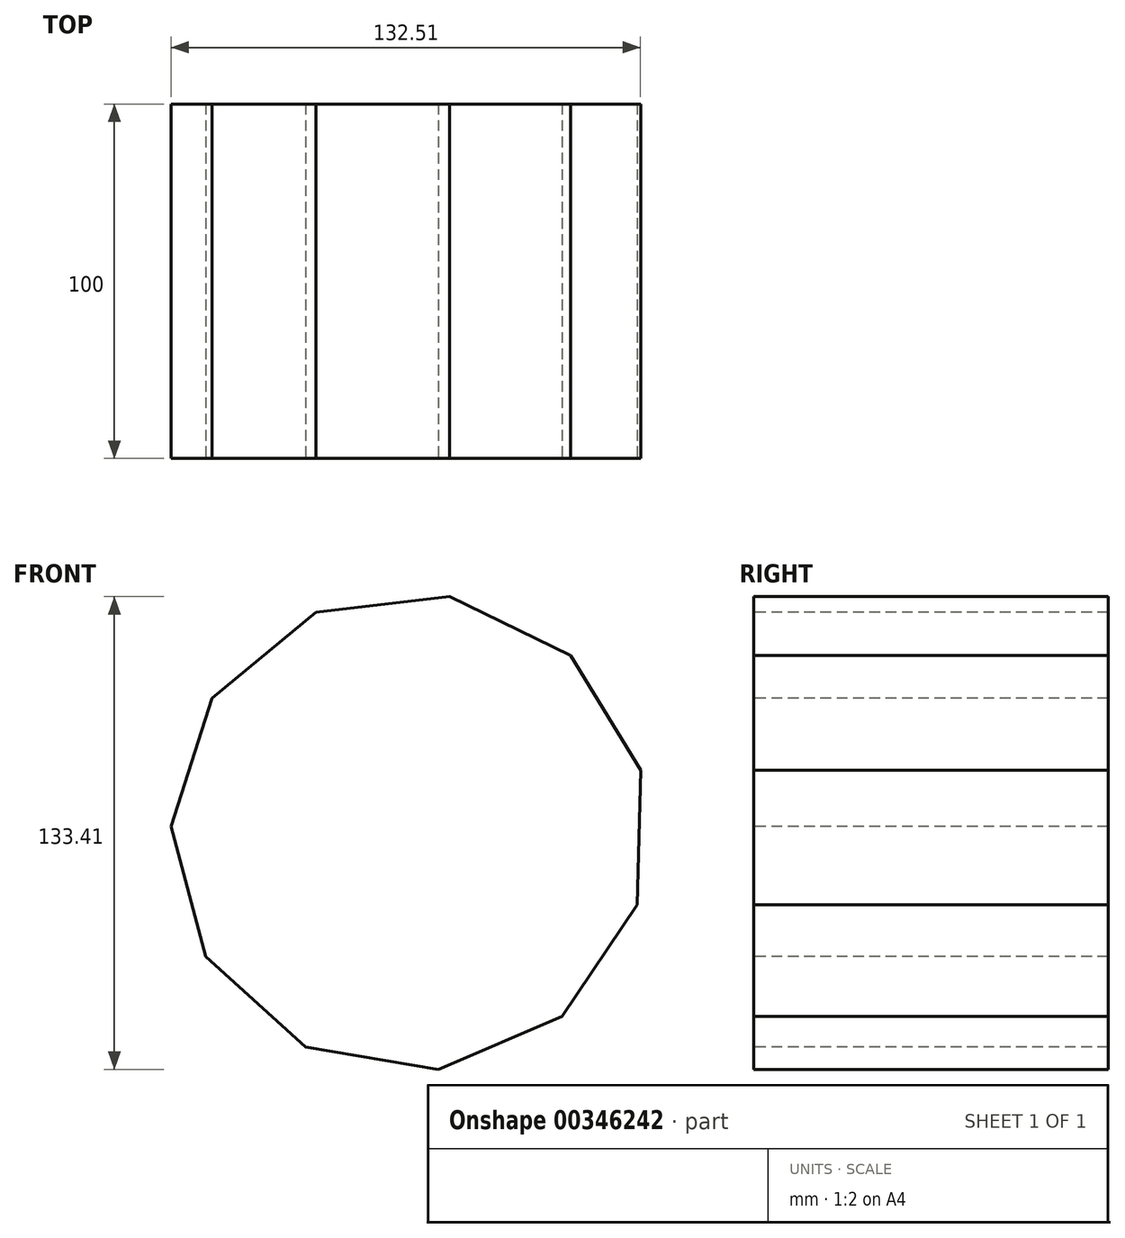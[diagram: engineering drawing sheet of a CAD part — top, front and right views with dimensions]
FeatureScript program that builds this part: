
annotation { "Feature Type Name" : "Feature", "Feature Type Description" : "" }
export const myFeature = defineFeature(function(context is Context, id is Id, definition is map)
    precondition{}
    {
        {
            var Q0;
            Q0=qCreatedBy(makeId("Front.planeOp"),FACE);
            var sketch = newSketch(context, id + "F0", { "sketchPlane" : qUnion([Q0])});
            skCircle(sketch, "E0.cCircle", {"center": v(0, 0) * mm, "radius": 67.41 * mm, "construction": true});
            skLineSegment(sketch, "E0.0", {"start": v(45.37, 49.86) * mm, "end": v(65.12, 17.42) * mm});
            skLineSegment(sketch, "E0.1", {"start": v(65.12, 17.42) * mm, "end": v(64.2, -20.55) * mm});
            skLineSegment(sketch, "E0.2", {"start": v(64.2, -20.55) * mm, "end": v(42.9, -52) * mm});
            skLineSegment(sketch, "E0.3", {"start": v(42.9, -52) * mm, "end": v(7.97, -66.94) * mm});
            skLineSegment(sketch, "E0.4", {"start": v(7.97, -66.94) * mm, "end": v(-29.48, -60.62) * mm});
            skLineSegment(sketch, "E0.5", {"start": v(-29.48, -60.62) * mm, "end": v(-57.58, -35.06) * mm});
            skLineSegment(sketch, "E0.6", {"start": v(-57.58, -35.06) * mm, "end": v(-67.4, 1.63) * mm});
            skLineSegment(sketch, "E0.7", {"start": v(-67.4, 1.63) * mm, "end": v(-55.8, 37.8) * mm});
            skLineSegment(sketch, "E0.8", {"start": v(-55.8, 37.8) * mm, "end": v(-26.5, 61.98) * mm});
            skLineSegment(sketch, "E0.9", {"start": v(-26.5, 61.98) * mm, "end": v(11.2, 66.47) * mm});
            skLineSegment(sketch, "E0.10", {"start": v(11.2, 66.47) * mm, "end": v(45.37, 49.86) * mm});
            skSolve(sketch);
        }
        {
            var Q0;
            Q0=makeQuery(id+"F0.imprint","IMPRINT",FACE,{"disambiguationData":[TD([[makeQuery(id+"F0.imprint","IMPRINT",EDGE,{"derivedFrom":sQuery(id+"F0.wireOp",EDGE,"E0.0")}),-1.0]])]});
            extrude(context, id + "F1", {"entities" : qUnion([Q0]), "oppositeDirection" : true, "depth" : 100 * mm});
        }
    });
